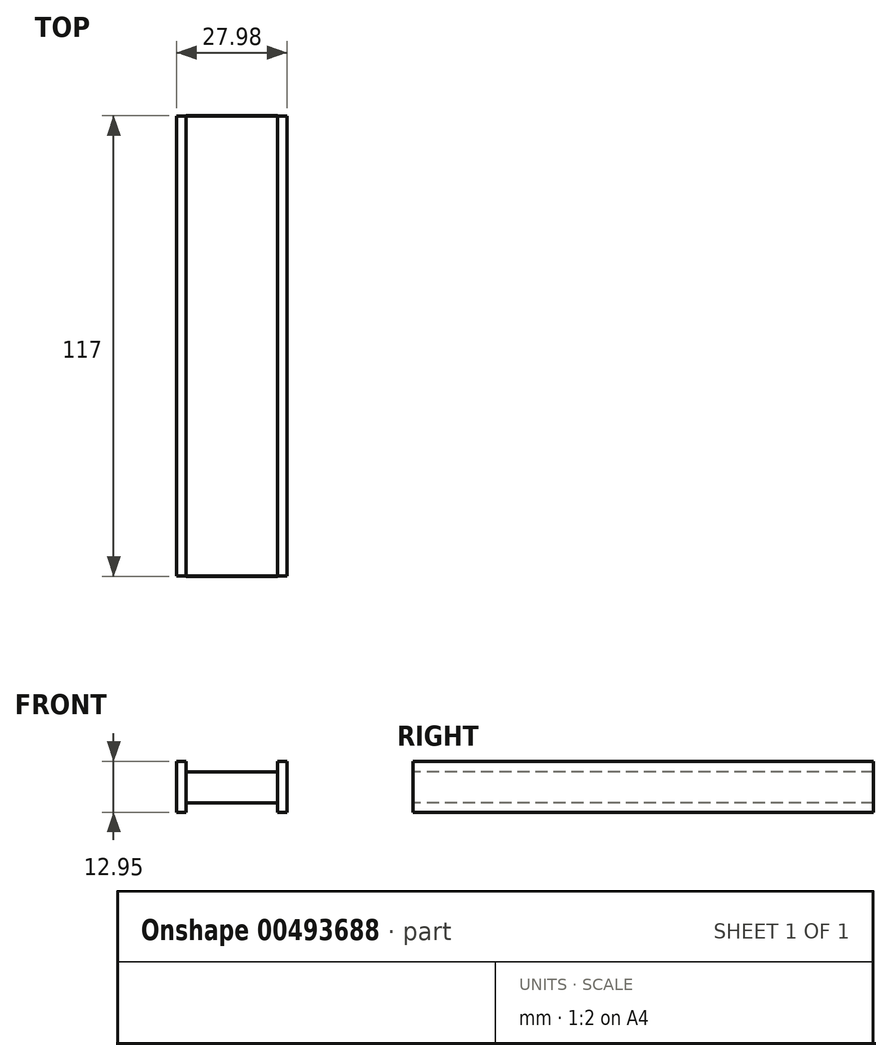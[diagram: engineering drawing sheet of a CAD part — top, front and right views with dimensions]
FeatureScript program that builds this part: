
annotation { "Feature Type Name" : "Feature", "Feature Type Description" : "" }
export const myFeature = defineFeature(function(context is Context, id is Id, definition is map)
    precondition{}
    {
        {
            var Q0;
            Q0=qCreatedBy(makeId("Top.planeOp"),FACE);
            var sketch = newSketch(context, id + "F0", { "sketchPlane" : qUnion([Q0])});
            skLineSegment(sketch, "E0.bottom", {"start": v(11.59, -58.5) * mm, "end": v(-11.59, -58.5) * mm});
            skLineSegment(sketch, "E0.top", {"start": v(11.59, 58.5) * mm, "end": v(-11.59, 58.5) * mm});
            skLineSegment(sketch, "E0.left", {"start": v(11.59, -58.5) * mm, "end": v(11.59, 58.5) * mm});
            skLineSegment(sketch, "E0.right", {"start": v(-11.59, -58.5) * mm, "end": v(-11.59, 58.5) * mm});
            skPoint(sketch, "E0.middle", {"position": v(0, 0) * mm});
            skSolve(sketch);
        }
        {
            var Q0;
            Q0=qCreatedBy(makeId("Top.planeOp"),FACE);
            var sketch = newSketch(context, id + "F1", { "sketchPlane" : qUnion([Q0])});
            skLineSegment(sketch, "E1.bottom", {"start": v(14, -58.44) * mm, "end": v(-14, -58.44) * mm});
            skLineSegment(sketch, "E1.top", {"start": v(14, 58.44) * mm, "end": v(-14, 58.44) * mm});
            skLineSegment(sketch, "E1.left", {"start": v(14, -58.44) * mm, "end": v(14, 58.44) * mm});
            skLineSegment(sketch, "E1.right", {"start": v(-14, -58.44) * mm, "end": v(-14, 58.44) * mm});
            skPoint(sketch, "E1.middle", {"position": v(0, 0) * mm});
            skSolve(sketch);
        }
        {
            var Q0;
            Q0 = qSketchRegion(id + "F1", true);
            var Q1;
            Q1=makeQuery(id+"F0.imprint","IMPRINT",FACE,{"disambiguationData":[TD([[makeQuery(id+"F0.imprint","IMPRINT",EDGE,{"derivedFrom":sQuery(id+"F0.wireOp",EDGE,"E0.bottom")}),-1.0]])]});
            extrude(context, id + "F2", {"entities" : qUnion([Q0, Q1]), "depth" : 12.95 * mm});
        }
        {
            var Q0;
            Q0=qCreatedBy(makeId("Front.planeOp"),FACE);
            var sketch = newSketch(context, id + "F3", { "sketchPlane" : qUnion([Q0])});
            skLineSegment(sketch, "E2.bottom", {"start": v(11.59, 2.2) * mm, "end": v(-11.59, 2.2) * mm});
            skLineSegment(sketch, "E2.top", {"start": v(11.59, 10.06) * mm, "end": v(-11.59, 10.06) * mm});
            skLineSegment(sketch, "E2.left", {"start": v(11.59, 2.2) * mm, "end": v(11.59, 10.06) * mm});
            skLineSegment(sketch, "E2.right", {"start": v(-11.59, 2.2) * mm, "end": v(-11.59, 10.06) * mm});
            skPoint(sketch, "E2.middle", {"position": v(0, 6.13) * mm});
            skSolve(sketch);
        }
        {
            var Q0;
            Q0=makeQuery(id+"F2.opExtrude","SWEPT_FACE",FACE,{"disambiguationData":[OSD([sQuery(id+"F0.wireOp",EDGE,"E0.bottom")])]});
            var sketch = newSketch(context, id + "F4", { "sketchPlane" : qUnion([Q0])});
            skLineSegment(sketch, "E3.bottom", {"start": v(11.59, 2.39) * mm, "end": v(-11.59, 2.39) * mm});
            skLineSegment(sketch, "E3.top", {"start": v(11.59, 10.24) * mm, "end": v(-11.59, 10.24) * mm});
            skLineSegment(sketch, "E3.left", {"start": v(11.59, 2.39) * mm, "end": v(11.59, 10.24) * mm});
            skLineSegment(sketch, "E3.right", {"start": v(-11.59, 2.39) * mm, "end": v(-11.59, 10.24) * mm});
            skPoint(sketch, "E3.middle", {"position": v(0, 6.31) * mm});
            skSolve(sketch);
        }
        {
            var Q0;
            {var subQ0=sQuery(id+"F4.wireOp",EDGE,"E3.top");Q0=makeQuery(id+"F4.imprint","IMPRINT",FACE,{"disambiguationData":[TD([[makeQuery(id+"F4.imprint","IMPRINT",EDGE,{"derivedFrom":subQ0}),-1.0]])]});}
            var Q1;
            {var subQ0=sQuery(id+"F4.wireOp",EDGE,"E3.bottom");Q1=makeQuery(id+"F4.imprint","IMPRINT",FACE,{"disambiguationData":[TD([[makeQuery(id+"F4.imprint","IMPRINT",EDGE,{"derivedFrom":subQ0}),1.0]])]});}
            extrude(context, id + "F5", {"entities" : qUnion([Q0, Q1]), "operationType" : NewBodyOperationType.REMOVE, "oppositeDirection" : true, "depth" : 117 * mm});
        }
    });
